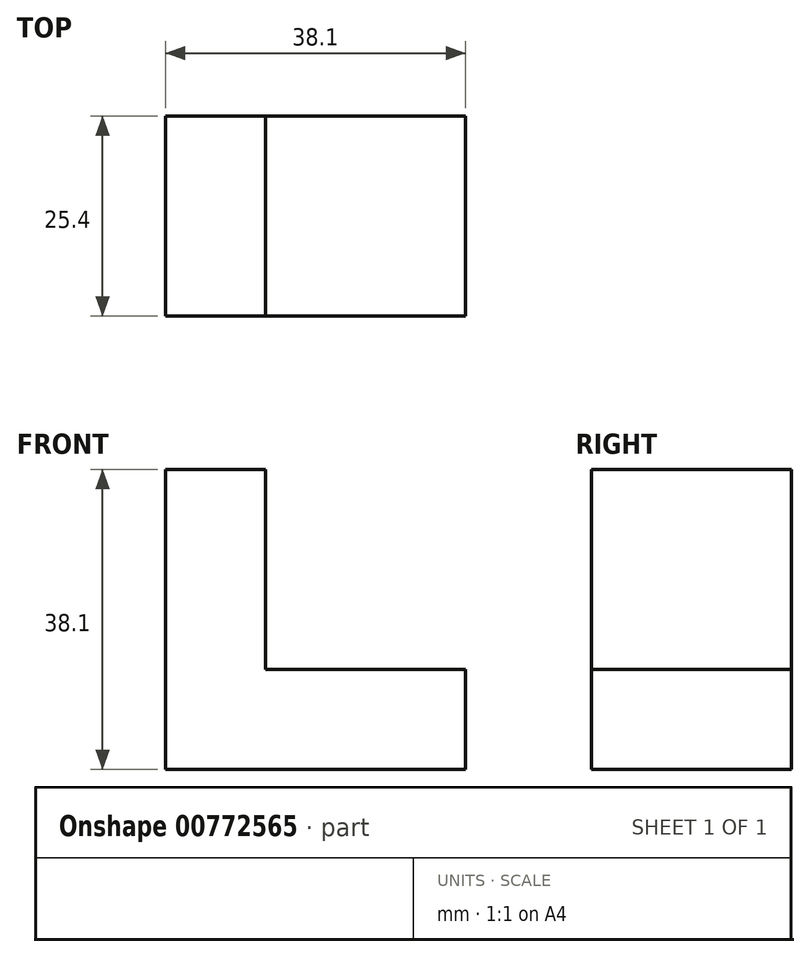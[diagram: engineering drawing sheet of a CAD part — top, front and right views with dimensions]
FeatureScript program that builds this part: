
annotation { "Feature Type Name" : "Feature", "Feature Type Description" : "" }
export const myFeature = defineFeature(function(context is Context, id is Id, definition is map)
    precondition{}
    {
        {
            var Q0;
            Q0=qCreatedBy(makeId("Front.planeOp"),FACE);
            var sketch = newSketch(context, id + "F0", { "sketchPlane" : qUnion([Q0])});
            skLineSegment(sketch, "E0", {"start": v(38.1, 0) * mm, "end": v(0, 0) * mm});
            skLineSegment(sketch, "E1", {"start": v(38.1, 0) * mm, "end": v(38.1, 12.7) * mm});
            skLineSegment(sketch, "E2", {"start": v(38.1, 12.7) * mm, "end": v(12.7, 12.7) * mm});
            skLineSegment(sketch, "E3", {"start": v(12.7, 12.7) * mm, "end": v(12.7, 38.1) * mm});
            skLineSegment(sketch, "E4", {"start": v(12.7, 38.1) * mm, "end": v(0, 38.1) * mm});
            skLineSegment(sketch, "E5", {"start": v(0, 38.1) * mm, "end": v(0, 0) * mm});
            skSolve(sketch);
        }
        {
            var Q0;
            Q0 = qSketchRegion(id + "F0", true);
            extrude(context, id + "F1", {"entities" : qUnion([Q0]), "depth" : 25.4 * mm, "offsetDistance" : 25.4 * mm});
        }
    });
